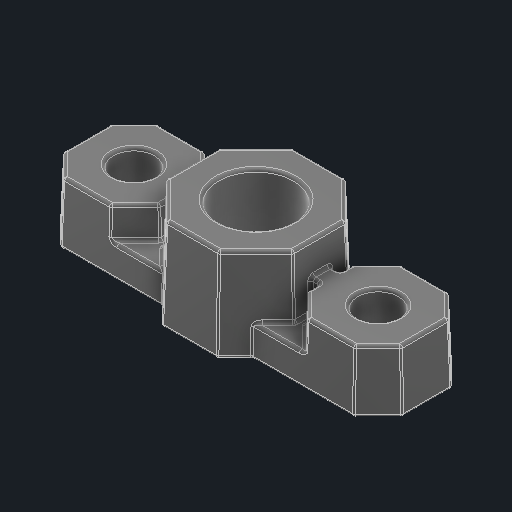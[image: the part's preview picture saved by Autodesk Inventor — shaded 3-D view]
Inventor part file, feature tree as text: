
AUTODESK INVENTOR PART (.ipt)
format: ipt  version: 2025 (Build 290162000, 162)  size: 823,296 bytes
history: native  units: in
note: dims shown in document units (in); Inventor stores cm internally (conversion verified against a paired STEP export)
features: other x8, fillet x2
ambient origin geometry x8: Origin, YZ Plane, XZ Plane, XY Plane, X Axis, Y Axis, Z Axis, Center Point
bodies: Body1 (feature_tree)
feature tree (10):
  other  "HS Bearing Flat.ipt"
  fillet  "Fillet7::HS Bearing Flat.ipt"  Radius=0.3937in
  other  "TaggingFeature1"
  fillet  "Fillet7"  [1 undecoded]
  other  "iInsert:6"
  other  "iInsert:3"
  other  "iInsert:5"
  other  "iInsert:1"
  other  "iInsert:2"
  other  "iInsert:4"
note: 1 required parameter value undecoded (feature->parameter linkage not recoverable at this tier; creation-order binding heuristic only, values carry confidence <= 0.55)
